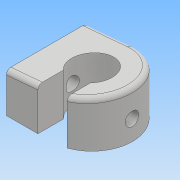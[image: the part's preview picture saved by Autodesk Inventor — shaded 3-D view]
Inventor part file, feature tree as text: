
AUTODESK INVENTOR PART (.ipt)
format: ipt  version: 2017 (Build 210142000, 142)  size: 171,520 bytes
history: native  units: mm
features: extrude x6, sketch x6, fillet x1
ambient origin geometry x8: Origin, YZ Plane, XZ Plane, XY Plane, X Axis, Y Axis, Z Axis, Center Point
bodies: Solid1 (feature_tree)
feature tree (13):
  extrude  "Extrusion1"  Depth=18.0mm
  extrude  "Extrusion2"  Depth=21.0mm
  extrude  "Extrusion3"  Depth=21.0mm
  extrude  "Extrusion4"  Depth=12.0mm TaperAngle=0.0deg
  extrude  "Extrusion5"  Depth=6.0mm
  fillet  "Fillet1"  Radius=12.0mm
  extrude  "Extrusion6"  Depth=1.0mm
  sketch  "Sketch1"  dims[d0=114.0mm d1=18.0mm]
  sketch  "Sketch2"  dims[d2=9.0mm d3=21.0mm]
  sketch  "Sketch3"  dims[d4=10.5mm d5=21.0mm]
  sketch  "Sketch4"  dims[d6=9.0mm d7=12.0mm d8=0.0mm]
  sketch  "Sketch5"  dims[d9=6.0mm d10=6.0mm d11=12.0mm d12=0.0mm]
  sketch  "Sketch6"  dims[d13=8.0mm d14=59.5mm d15=30.543262mm d16=12.0mm d17=0.0mm d18=114.5mm d19=21.0mm d20=12.0mm d21=0.0mm d23=12.0mm d24=0.0mm d25=1.0mm d26=3.0mm d27=5.0mm d28=0.0mm d29=3.0mm]
